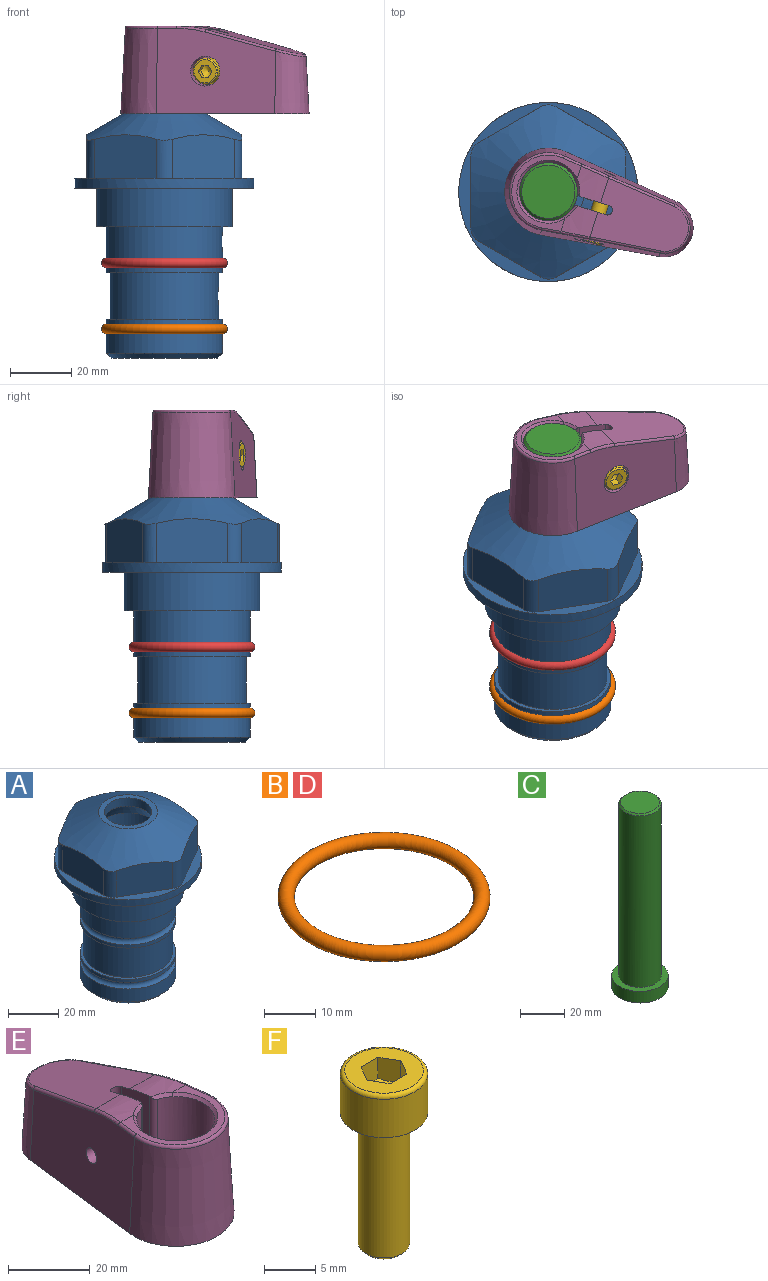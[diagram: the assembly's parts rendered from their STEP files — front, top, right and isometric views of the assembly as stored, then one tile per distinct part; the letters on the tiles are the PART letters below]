
ASSEMBLY  parts=6 mates=5
PART A: 36 faces, bbox 58.7x58.7x81 mm
  f0: cylinder r=17.78mm len=35.56mm, axis (0,0,1), area 1670.8mm2, adj f23,f24,f31
  f1: cylinder r=19.05mm len=38.1mm, axis (0,0,1), area 1191.9mm2, adj f26,f27,f30
  f2: plane 58.66x58.66mm, normal (0,0,-1), area 1150.6mm2, adj f3,f28
  f3: cylinder r=29.33mm len=58.66mm, axis (0,0,-1), area 585.1mm2, adj f2,f4
  f4: plane 58.66x58.66mm, normal (0,0,1), area 475.9mm2, adj f3,f5,f6,f7,f8,f9,f10,f11
  f5: plane 20.32x14.34mm, normal (-0.5,0.87,0), area 324.4mm2, adj f4,f15,f16,f17
  f6: plane 20.32x14.34mm, normal (0.5,0.87,0), area 324.4mm2, adj f4,f14,f15,f17
  f7: plane 23.48x14.34mm, normal (1,0,0), area 324.4mm2, adj f4,f13,f14,f17
  f8: plane 20.32x14.34mm, normal (0.5,-0.87,0), area 324.4mm2, adj f4,f12,f13,f17
  f9: plane 20.32x14.34mm, normal (-0.5,-0.87,0), area 324.4mm2, adj f4,f11,f12,f17
  f10: plane 23.48x14.34mm, normal (-1,0,0), area 324.4mm2, adj f4,f11,f16,f17
  f11: cylinder r=5.08mm len=12.85mm, axis (0,0,-1), area 67.2mm2, adj f4,f9,f10,f17
  f12: cylinder r=5.08mm len=12.85mm, axis (0,0,-1), area 67.2mm2, adj f4,f8,f9,f17
  f13: cylinder r=5.08mm len=12.85mm, axis (0,0,-1), area 67.2mm2, adj f4,f7,f8,f17
  f14: cylinder r=5.08mm len=12.85mm, axis (0,0,-1), area 67.2mm2, adj f4,f6,f7,f17
  f15: cylinder r=5.08mm len=12.85mm, axis (0,0,-1), area 67.2mm2, adj f4,f5,f6,f17
  f16: cylinder r=5.08mm len=12.85mm, axis (0,0,-1), area 67.2mm2, adj f4,f5,f10,f17
  f17: cone r=11.73mm half-angle=60deg, axis (0,0,-1), area 2071.8mm2, adj f5,f6,f7,f8,f9,f10,f11,f12
  f18: plane 23.46x23.46mm, normal (0,0,1), area 147.4mm2, adj f17,f35
  f19: plane 34.93x34.93mm, normal (0,0,-1), area 958mm2, adj f29
  f20: cylinder r=19.05mm len=38.1mm, axis (0,0,1), area 760.1mm2, adj f21,f29
  f21: torus R=19.05mm, axis (0,0,1), area 565.3mm2, adj f20,f22
  f22: cylinder r=19.05mm len=38.1mm, axis (0,0,1), area 190mm2, adj f21,f23
  f23: plane 38.1x38.1mm, normal (0,0,1), area 146.9mm2, adj f0,f22
  f24: plane 38.1x38.1mm, normal (0,0,-1), area 146.9mm2, adj f0,f25
  f25: cylinder r=19.05mm len=38.1mm, axis (0,0,1), area 190mm2, adj f24,f26
  f26: torus R=19.05mm, axis (0,0,1), area 565.3mm2, adj f1,f25
  f27: plane 44.45x44.45mm, normal (0,0,-1), area 411.7mm2, adj f1,f28
  f28: cylinder r=22.23mm len=44.45mm, axis (0,0,1), area 1773.5mm2, adj f2,f27
  f29: cone r=19.05mm half-angle=45deg, axis (0,0,1), area 257.5mm2, adj f19,f20
  f30: cylinder r=3.17mm len=6.75mm, axis (-1,0,0), area 128mm2, adj f1,f33
  f31: cylinder r=3.17mm len=6.35mm, axis (-1,0,0), area 102.5mm2, adj f0,f33
  f32: plane 25.4x25.4mm, normal (0,0,1), area 506.7mm2, adj f33
  f33: cylinder r=12.7mm len=66.42mm, axis (0,0,-1), area 5236.2mm2, adj f30,f31,f32,f34
  f34: cone r=9.53mm half-angle=30deg, axis (0,0,-1), area 443.4mm2, adj f33,f35
  f35: cylinder r=9.53mm len=19.05mm, axis (0,0,-1), area 240.9mm2, adj f18,f34
PART B: 1 faces, bbox 44.7x44.7x3.2 mm
  f0: torus R=19.05mm, axis (0,0,1), area 1193.9mm2
PART C: 6 faces, bbox 25.4x25.4x101.6 mm
  f0: plane 17.46x17.46mm, normal (0,0,1), area 239.5mm2, adj f5
  f1: plane 25.4x25.4mm, normal (0,0,-1), area 506.7mm2, adj f2
  f2: cylinder r=12.7mm len=25.4mm, axis (0,0,1), area 506.7mm2, adj f1,f3
  f3: plane 25.4x25.4mm, normal (0,0,1), area 221.7mm2, adj f2,f4
  f4: cylinder r=9.53mm len=94.46mm, axis (0,0,1), area 5653mm2, adj f3,f5
  f5: cone r=8.73mm half-angle=45deg, axis (0,0,-1), area 64.4mm2, adj f0,f4
PART D: same geometry as B
PART E: 47 faces, bbox 30.7x65.6x30.9 mm
  f0: plane 27.86x20.29mm, normal (-0.99,-0.12,-0.09), area 300.3mm2, adj f1,f2,f3,f4,f41,f42,f43,f45
  f1: cylinder r=9.96mm len=5.92mm, axis (1,0,0), area 1.7mm2, adj f0,f2,f46
  f2: cylinder r=14.61mm len=2.45mm, axis (0,0,-1), area 2mm2, adj f0,f1,f3,f46
  f3: cone r=13.91mm half-angle=45deg, axis (0,0,-1), area 3.5mm2, adj f0,f2,f4,f46
  f4: plane 63.5x28.58mm, normal (0,0,-1), area 861.2mm2, adj f0,f3,f5,f22,f26,f27,f28,f29
  f5: cylinder r=1.59mm len=26.75mm, axis (0,0,-1), area 133.4mm2, adj f4,f6,f22,f29
  f6: plane 31.05x21.04mm, normal (0,0.26,0.97), area 496.7mm2, adj f5,f7,f18,f19,f20,f21,f22,f29
  f7: cylinder r=0.79mm len=23.49mm, axis (0.1,-0.96,0.26), area 28.7mm2, adj f6,f8,f21,f33
  f8: bspline ~9.68x2mm, area 11.6mm2, adj f7,f9,f18,f33
  f9: cylinder r=0.79mm len=6.43mm, axis (0.12,-0.99,0), area 7.7mm2, adj f8,f10,f17,f33
  f10: plane 24.05x19.81mm, normal (0,0,1), area 97.3mm2, adj f9,f11,f15,f17,f18,f19
  f11: cone r=9.53mm half-angle=45deg, axis (0,0,1), area 54mm2, adj f10,f12,f13,f14
  f12: bspline ~5.57x3.11mm, area 5.6mm2, adj f11,f13,f18,f26
  f13: cylinder r=9.53mm len=27.2mm, axis (0,0,-1), area 1477.5mm2, adj f11,f12,f14,f26,f27,f28
  f14: bspline ~5.57x3.11mm, area 5.6mm2, adj f11,f13,f19,f28
  f15: cylinder r=0.79mm len=6.43mm, axis (-0.12,-0.99,0), area 7.7mm2, adj f10,f16,f17,f31
  f16: bspline ~9.68x2mm, area 11.6mm2, adj f15,f19,f20,f31
  f17: torus R=12.03mm, axis (0,0,1), area 51mm2, adj f9,f10,f15,f32
  f18: cylinder r=37.35mm len=9.67mm, axis (1,0,0), area 80.5mm2, adj f6,f8,f10,f12,f22,f26
  f19: cylinder r=37.35mm len=9.67mm, axis (1,0,0), area 80.5mm2, adj f6,f10,f14,f16,f28,f29
  f20: cylinder r=0.79mm len=23.49mm, axis (-0.1,-0.96,0.26), area 28.7mm2, adj f6,f16,f21,f31
  f21: bspline ~16.78x7.53mm, area 25.7mm2, adj f6,f7,f20,f34
  f22: plane 28.68x9.67mm, normal (-1,0,0), area 256.5mm2, adj f4,f5,f6,f18,f23,f26
  f23: cylinder r=2.05mm len=5.09mm, axis (1,0,0), area 65.5mm2, adj f22,f24
  f24: plane 9.75x9.75mm, normal (1,0,0), area 61.5mm2, adj f23,f25
  f25: cylinder r=4.88mm len=9.75mm, axis (1,0,0), area 162.4mm2, adj f24,f33
  f26: cylinder r=1.59mm len=28.71mm, axis (0,0,-1), area 57.1mm2, adj f4,f12,f13,f18,f22,f27
  f27: cone r=10.32mm half-angle=45deg, axis (0,0,-1), area 65mm2, adj f4,f13,f26,f28
  f28: cylinder r=1.59mm len=28.71mm, axis (0,0,-1), area 57.1mm2, adj f4,f13,f14,f19,f27,f29
  f29: plane 28.68x9.67mm, normal (1,0,0), area 256.5mm2, adj f4,f5,f6,f19,f28,f30
  f30: cylinder r=2.05mm len=10.19mm, axis (1,0,0), area 127.9mm2, adj f29,f31
  f31: plane 39.54x28.28mm, normal (-0.99,0.12,0.05), area 986mm2, adj f4,f15,f16,f20,f30,f32,f34
  f32: cone r=14.29mm half-angle=3deg, axis (0,0,-1), area 1286.9mm2, adj f4,f17,f31,f33
  f33: plane 41.4x30.14mm, normal (0.99,0.12,0.05), area 924mm2, adj f4,f7,f8,f9,f25,f32,f34
  f34: cone r=9.53mm half-angle=3deg, axis (0,0,-1), area 507.1mm2, adj f4,f21,f31,f33
  f35: plane 27.92x20.38mm, normal (0.99,-0.12,-0.09), area 344.6mm2, adj f4,f36,f37,f38,f39,f40,f41,f42
  f36: cylinder r=7.13mm len=2.54mm, axis (1,0,0), area 0mm2, adj f35,f45
  f37: cylinder r=14.61mm len=5.78mm, axis (0,0,-1), area 3.7mm2, adj f35,f38,f39,f40
  f38: cylinder r=7.13mm len=3.66mm, axis (1,0,0), area 0.6mm2, adj f35,f37,f39
  f39: plane 8.67x7.45mm, normal (-1,0,0), area 38.4mm2, adj f4,f35,f37,f38,f40,f45
  f40: cone r=13.91mm half-angle=45deg, axis (0,0,-1), area 3.5mm2, adj f4,f35,f37,f39
  f41: cone r=4.45mm half-angle=5deg, axis (0,0,-1), area 176.3mm2, adj f0,f4,f35,f42
  f42: plane 18.95x10.34mm, normal (0,-0.26,-0.97), area 116.1mm2, adj f0,f35,f41,f43,f45
  f43: cylinder r=9.96mm len=14.23mm, axis (1,0,0), area 35.7mm2, adj f0,f42,f44,f45
  f44: plane 7.59x0.75mm, normal (-1,0,0), area 3.8mm2, adj f43,f45
  f45: cylinder r=6.67mm len=20.16mm, axis (0,0,-1), area 224.8mm2, adj f0,f4,f35,f36,f39,f42,f43,f44
  f46: plane 7.45x5.29mm, normal (1,0,0), area 24.7mm2, adj f0,f1,f2,f3,f4,f45
PART F: 18 faces, bbox 9.2x9.2x21 mm
  f0: cone r=2.28mm half-angle=45deg, axis (0,0,1), area 8.8mm2, adj f1,f16
  f1: cylinder r=2.5mm len=14.83mm, axis (0,0,-1), area 233mm2, adj f0,f15
  f2: cone r=2.28mm half-angle=45deg, axis (0,0,1), area 8.8mm2, adj f3,f15
  f3: cylinder r=2.5mm len=5mm, axis (0,0,-1), area 0.8mm2, adj f2,f4
  f4: torus R=2.75mm, axis (0,0,-1), area 6.4mm2, adj f3,f14
  f5: cylinder r=4.25mm len=8.5mm, axis (0,0,-1), area 122.2mm2, adj f6,f14
  f6: torus R=3.82mm, axis (0,0,-1), area 17.2mm2, adj f5,f17
  f7: cone r=1.15mm half-angle=60deg, axis (0,0,1), area 16mm2, adj f8,f9,f10,f11,f12,f13
  f8: plane 2.76x2mm, normal (0.87,0.5,0), area 6mm2, adj f7,f9,f13,f17
  f9: plane 2.76x2.31mm, normal (0,1,0), area 6mm2, adj f7,f8,f10,f17
  f10: plane 2.76x2mm, normal (-0.87,0.5,0), area 6mm2, adj f7,f9,f11,f17
  f11: plane 2.76x2mm, normal (-0.87,-0.5,0), area 6mm2, adj f7,f10,f12,f17
  f12: plane 2.71x2.31mm, normal (0,-1,0), area 6mm2, adj f7,f11,f13,f17
  f13: plane 2.76x2mm, normal (0.87,-0.5,0), area 6mm2, adj f7,f8,f12,f17
  f14: plane 8.5x8.5mm, normal (0,0,-1), area 33mm2, adj f4,f5
  f15: plane 5x5mm, normal (0,0,1), area 6.2mm2, adj f1,f2
  f16: plane 4.13x4.13mm, normal (0,0,-1), area 13.4mm2, adj f0
  f17: plane 7.65x7.65mm, normal (0,0,1), area 32.1mm2, adj f6,f8,f9,f10,f11,f12,f13
PLACE A at identity fixed
PLACE B rot(axis=(1,0,0),0deg) t=(0,0,-21.59)mm
PLACE C rot(axis=(0,0,1),162.7deg) t=(0,0,-10.38)mm
PLACE D at identity
PLACE E rot(axis=(0,0,-1),107.3deg) t=(0,0,24.34)mm
PLACE F rot(axis=(-0.11,-0.7,0.7),167.8deg) t=(14.81,-11.6,38.33)mm
MATE cylindrical C.f2 <-> A.f0  axis (0,0,1) through (0,0,-42.13)mm
MATE fastened D.f0 <-> A.f0  axis (0,0,1) through (0,0,-24.51)mm
MATE fastened B.f0 <-> A.f0  axis (0,0,1) through (0,0,-46.1)mm
MATE fastened E.f2 <-> C.f2  axis (0,0,1) through (0,0,53.12)mm
MATE fastened F.f7 <-> E.f1  axis (0.3,0.95,0) through (14.81,-11.6,38.33)mm
